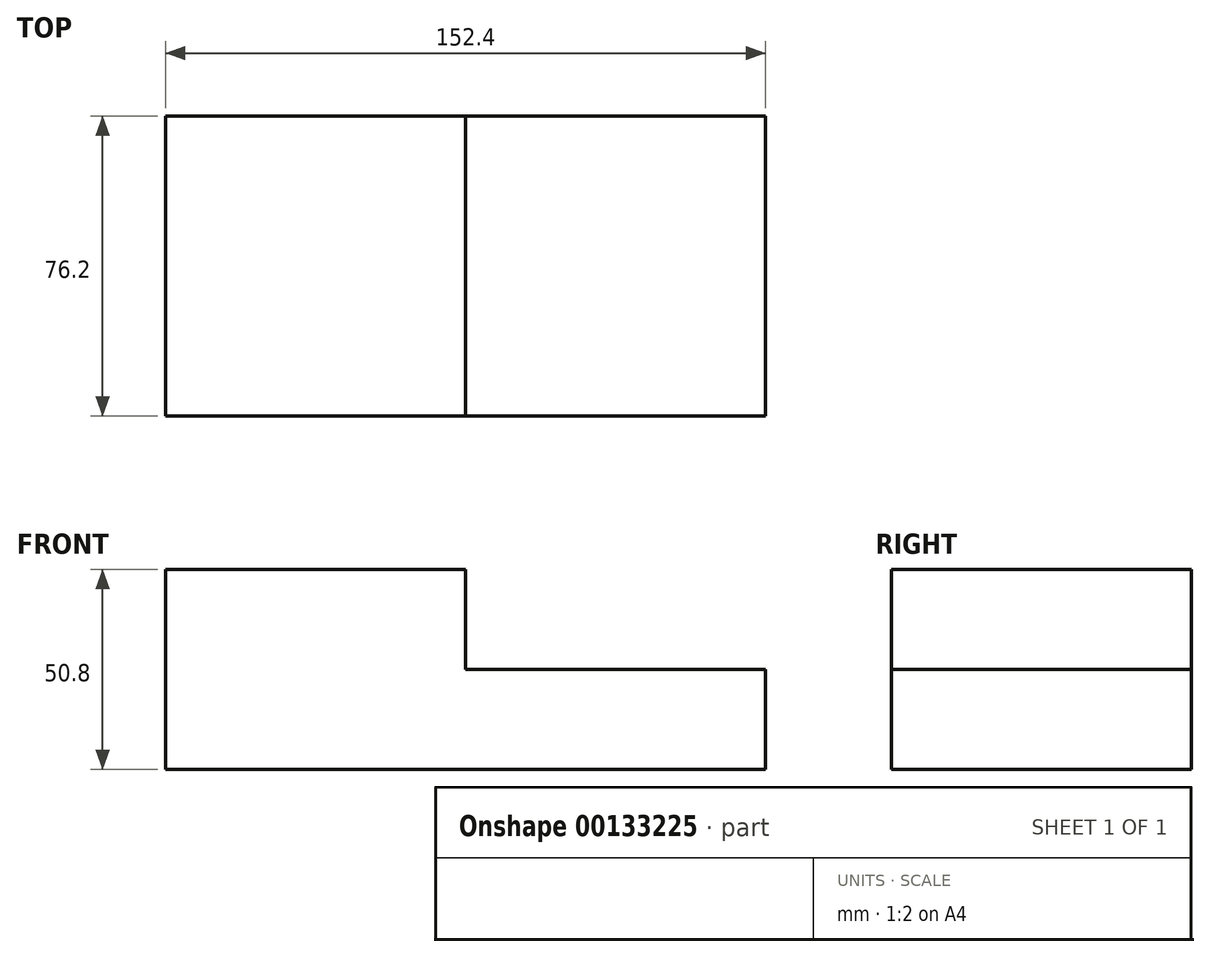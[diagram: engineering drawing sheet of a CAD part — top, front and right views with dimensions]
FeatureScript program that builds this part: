
annotation { "Feature Type Name" : "Feature", "Feature Type Description" : "" }
export const myFeature = defineFeature(function(context is Context, id is Id, definition is map)
    precondition{}
    {
        {
            var Q0;
            Q0=qCreatedBy(makeId("Front.planeOp"),FACE);
            var sketch = newSketch(context, id + "F0", { "sketchPlane" : qUnion([Q0])});
            skLineSegment(sketch, "E0.bottom", {"start": v(-76.2, 25.4) * mm, "end": v(0, 25.4) * mm});
            skLineSegment(sketch, "E0.top", {"start": v(-76.2, -25.4) * mm, "end": v(76.2, -25.4) * mm});
            skLineSegment(sketch, "E0.left", {"start": v(-76.2, 25.4) * mm, "end": v(-76.2, -25.4) * mm});
            skLineSegment(sketch, "E0.right", {"start": v(76.2, 0) * mm, "end": v(76.2, -25.4) * mm});
            skPoint(sketch, "E0.middle", {"position": v(0, 0) * mm});
            skLineSegment(sketch, "E1", {"start": v(0, 25.4) * mm, "end": v(0, 0) * mm});
            skLineSegment(sketch, "E2", {"start": v(76.2, 0) * mm, "end": v(0, 0) * mm});
            skSolve(sketch);
        }
        {
            var Q0;
            Q0 = qSketchRegion(id + "F0", true);
            extrude(context, id + "F1", {"entities" : qUnion([Q0]), "endBound" : BoundingType.SYMMETRIC, "depth" : 76.2 * mm});
        }
    });
